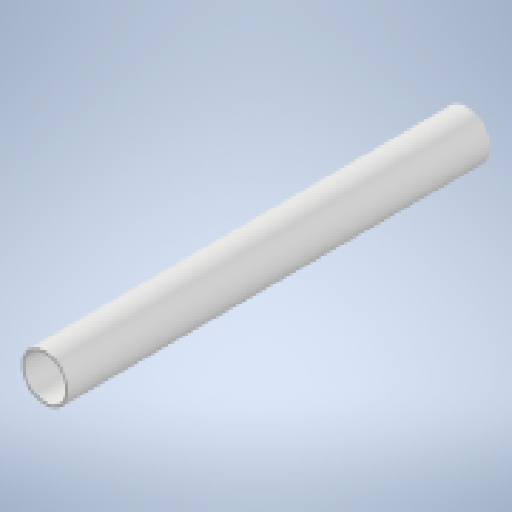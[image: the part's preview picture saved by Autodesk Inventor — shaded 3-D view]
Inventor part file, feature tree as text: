
AUTODESK INVENTOR PART (.ipt)
format: ipt  version: 2023.2 (Build 272271030, 271C)  size: 139,264 bytes
history: native  units: mm
features: extrude x1, sketch x1
ambient origin geometry x8: Origin, YZ Plane, XZ Plane, XY Plane, X Axis, Y Axis, Z Axis, Center Point
bodies: Solid1 (feature_tree)
feature tree (2):
  extrude  "Extrusion1"  Depth=300.0mm TaperAngle=0.0deg
  sketch  "Sketch1"  dims[d1=2.0mm d2=300.0mm d3=0.0mm d4=33.5mm]
